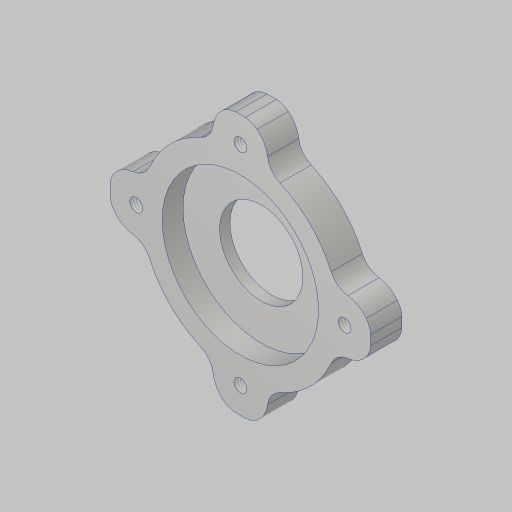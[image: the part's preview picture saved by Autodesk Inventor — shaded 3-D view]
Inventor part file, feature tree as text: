
AUTODESK INVENTOR PART (.ipt)
format: ipt  version: 2023.5 (Build 275446000, 446)  size: 281,600 bytes
history: native  units: in
note: dims shown in document units (in); Inventor stores cm internally (conversion verified against a paired STEP export)
features: extrude x3, sketch x2, hole x1, mirror x1, fillet x1, projected_geometry x1
ambient origin geometry x8: Origin, YZ Plane, XZ Plane, XY Plane, X Axis, Y Axis, Z Axis, Center Point
bodies: Solid1 (feature_tree)
feature tree (9):
  sketch  "Sketch1"  dims[d0=1.875in d1=0.625in]
  extrude  "Extrusion1"  Depth=0.625in
  extrude  "Extrusion2"  Depth=0.375in TaperAngle=0.0deg
  hole  "Hole1"  [1 undecoded]
  extrude  "Extrusion3"  Depth=0.25in TaperAngle=0.0deg
  mirror  "Mirror1"
  fillet  "Fillet1"  Radius=0.25in
  sketch  "Sketch2"  dims[d2=2.5in d3=0.375in d4=0.0in d5=1.0in d6=0.25in d7=0.0in d8=0.156in d9=0.38in d10=0.385in d11=0.25in d12=0.5635in d13=1.0in d14=0.8108in d15=0.25in d16=0.25in d17=0.25in d18=0.25in d19=0.25in d20=45.0deg d21=0.25in d22=45.0deg d23=0.25in d24=0.0in d25=0.25in d26=0.25in d27=0.25in]
  projected_geometry  "Project Cut Edges1"
note: 1 required parameter value undecoded (feature->parameter linkage not recoverable at this tier; creation-order binding heuristic only, values carry confidence <= 0.55)
